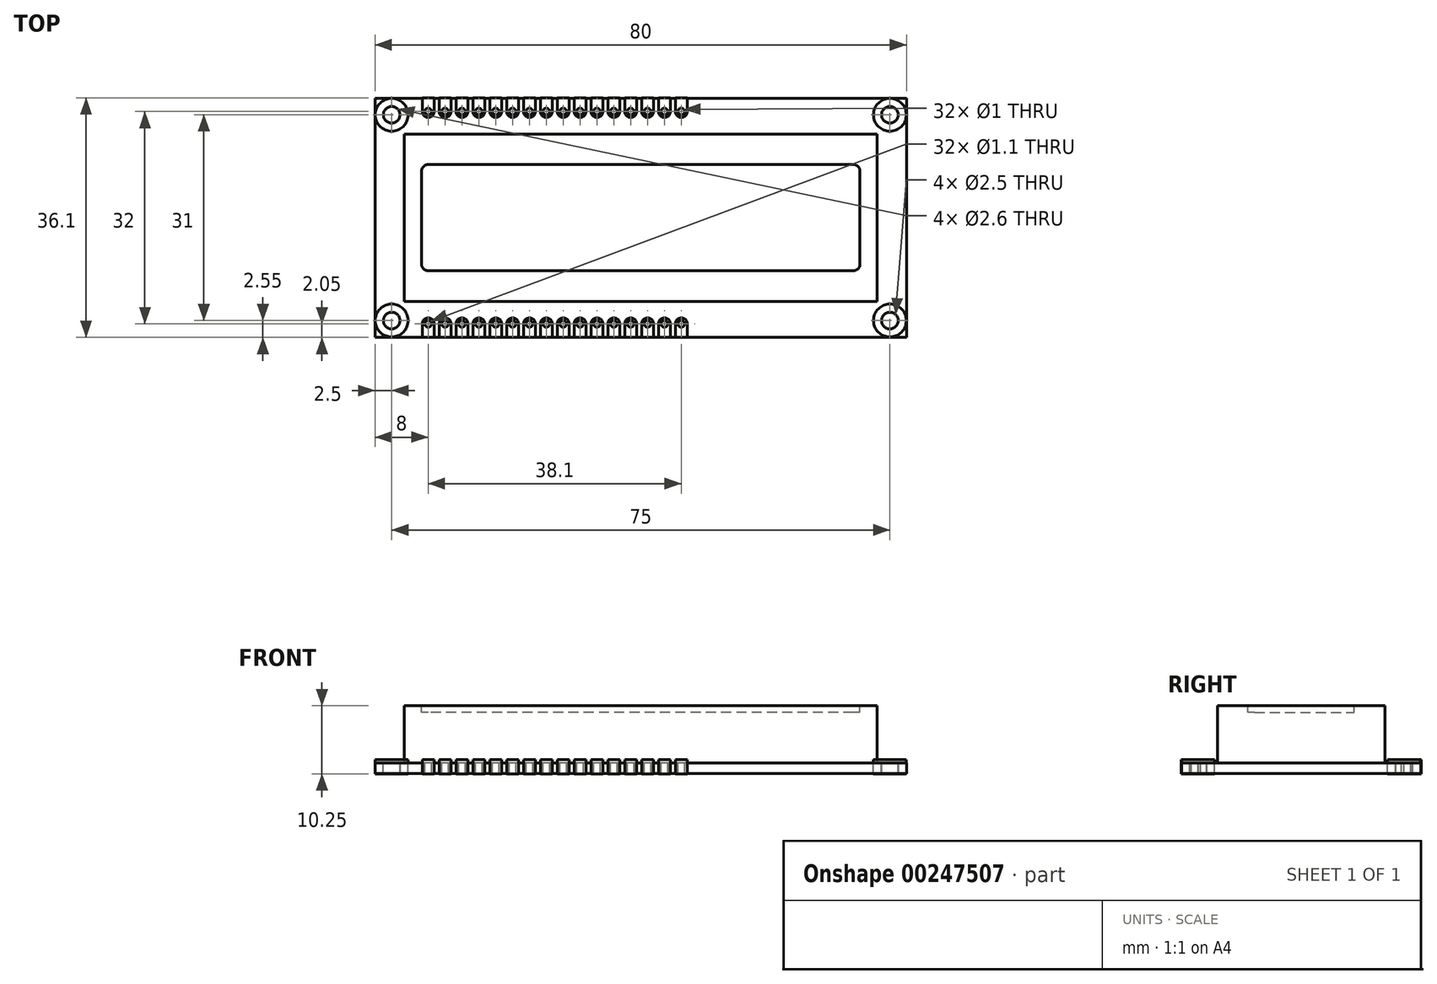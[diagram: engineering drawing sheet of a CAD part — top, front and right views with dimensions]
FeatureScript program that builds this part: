
annotation { "Feature Type Name" : "Feature", "Feature Type Description" : "" }
export const myFeature = defineFeature(function(context is Context, id is Id, definition is map)
    precondition{}
    {
        {
            var Q0;
            Q0=qCreatedBy(makeId("Top.planeOp"),FACE);
            var sketch = newSketch(context, id + "F0", { "sketchPlane" : qUnion([Q0])});
            skLineSegment(sketch, "E0.bottom", {"start": v(40, -18) * mm, "end": v(-40, -18) * mm});
            skLineSegment(sketch, "E0.top", {"start": v(40, 18) * mm, "end": v(-40, 18) * mm});
            skLineSegment(sketch, "E0.left", {"start": v(40, -18) * mm, "end": v(40, 18) * mm});
            skLineSegment(sketch, "E0.right", {"start": v(-40, -18) * mm, "end": v(-40, 18) * mm});
            skPoint(sketch, "E0.middle", {"position": v(0, 0) * mm});
            skSolve(sketch);
        }
        {
            var Q0;
            Q0 = qSketchRegion(id + "F0", true);
            extrude(context, id + "F1", {"entities" : qUnion([Q0]), "depth" : 1.6 * mm});
        }
        {
            var Q0;
            Q0=makeQuery(id+"F1.opExtrude","CAP_FACE",FACE,{"disambiguationData":[OSD([sQuery(id+"F0.wireOp",EDGE,"E0.bottom"),sQuery(id+"F0.wireOp",EDGE,"E0.top"),sQuery(id+"F0.wireOp",EDGE,"E0.left"),sQuery(id+"F0.wireOp",EDGE,"E0.right")])],"isStart":false});
            var sketch = newSketch(context, id + "F2", { "sketchPlane" : qUnion([Q0])});
            skCircle(sketch, "E1", {"center": v(-37.5, 15.5) * mm, "radius": 1.3 * mm});
            skCircle(sketch, "E2.0.1.0", {"center": v(-37.5, -15.5) * mm, "radius": 1.3 * mm});
            skCircle(sketch, "E2.1.0.0", {"center": v(37.5, 15.5) * mm, "radius": 1.3 * mm});
            skCircle(sketch, "E2.1.1.0", {"center": v(37.5, -15.5) * mm, "radius": 1.3 * mm});
            skLineSegment(sketch, "E2.direction1", {"start": v(-37.5, 15.5) * mm, "end": v(37.5, 15.5) * mm, "construction": true});
            skLineSegment(sketch, "E2.direction2", {"start": v(-37.5, 15.5) * mm, "end": v(-37.5, -15.5) * mm, "construction": true});
            skCircle(sketch, "E3", {"center": v(-32, 16) * mm, "radius": 0.55 * mm});
            skCircle(sketch, "E4.0.1.0", {"center": v(-32, -16) * mm, "radius": 0.55 * mm});
            skCircle(sketch, "E4.1.0.0", {"center": v(-29.46, 16) * mm, "radius": 0.55 * mm});
            skCircle(sketch, "E4.1.1.0", {"center": v(-29.46, -16) * mm, "radius": 0.55 * mm});
            skCircle(sketch, "E4.2.0.0", {"center": v(-26.92, 16) * mm, "radius": 0.55 * mm});
            skCircle(sketch, "E4.2.1.0", {"center": v(-26.92, -16) * mm, "radius": 0.55 * mm});
            skCircle(sketch, "E4.3.0.0", {"center": v(-24.38, 16) * mm, "radius": 0.55 * mm});
            skCircle(sketch, "E4.3.1.0", {"center": v(-24.38, -16) * mm, "radius": 0.55 * mm});
            skCircle(sketch, "E4.4.0.0", {"center": v(-21.84, 16) * mm, "radius": 0.55 * mm});
            skCircle(sketch, "E4.4.1.0", {"center": v(-21.84, -16) * mm, "radius": 0.55 * mm});
            skCircle(sketch, "E4.5.0.0", {"center": v(-19.3, 16) * mm, "radius": 0.55 * mm});
            skCircle(sketch, "E4.5.1.0", {"center": v(-19.3, -16) * mm, "radius": 0.55 * mm});
            skCircle(sketch, "E4.6.0.0", {"center": v(-16.76, 16) * mm, "radius": 0.55 * mm});
            skCircle(sketch, "E4.6.1.0", {"center": v(-16.76, -16) * mm, "radius": 0.55 * mm});
            skCircle(sketch, "E4.7.0.0", {"center": v(-14.22, 16) * mm, "radius": 0.55 * mm});
            skCircle(sketch, "E4.7.1.0", {"center": v(-14.22, -16) * mm, "radius": 0.55 * mm});
            skCircle(sketch, "E4.8.0.0", {"center": v(-11.68, 16) * mm, "radius": 0.55 * mm});
            skCircle(sketch, "E4.8.1.0", {"center": v(-11.68, -16) * mm, "radius": 0.55 * mm});
            skCircle(sketch, "E4.9.0.0", {"center": v(-9.14, 16) * mm, "radius": 0.55 * mm});
            skCircle(sketch, "E4.9.1.0", {"center": v(-9.14, -16) * mm, "radius": 0.55 * mm});
            skCircle(sketch, "E4.10.0.0", {"center": v(-6.6, 16) * mm, "radius": 0.55 * mm});
            skCircle(sketch, "E4.10.1.0", {"center": v(-6.6, -16) * mm, "radius": 0.55 * mm});
            skCircle(sketch, "E4.11.0.0", {"center": v(-4.06, 16) * mm, "radius": 0.55 * mm});
            skCircle(sketch, "E4.11.1.0", {"center": v(-4.06, -16) * mm, "radius": 0.55 * mm});
            skCircle(sketch, "E4.12.0.0", {"center": v(-1.52, 16) * mm, "radius": 0.55 * mm});
            skCircle(sketch, "E4.12.1.0", {"center": v(-1.52, -16) * mm, "radius": 0.55 * mm});
            skCircle(sketch, "E4.13.0.0", {"center": v(1.02, 16) * mm, "radius": 0.55 * mm});
            skCircle(sketch, "E4.13.1.0", {"center": v(1.02, -16) * mm, "radius": 0.55 * mm});
            skCircle(sketch, "E4.14.0.0", {"center": v(3.56, 16) * mm, "radius": 0.55 * mm});
            skCircle(sketch, "E4.14.1.0", {"center": v(3.56, -16) * mm, "radius": 0.55 * mm});
            skCircle(sketch, "E4.15.0.0", {"center": v(6.1, 16) * mm, "radius": 0.55 * mm});
            skCircle(sketch, "E4.15.1.0", {"center": v(6.1, -16) * mm, "radius": 0.55 * mm});
            skLineSegment(sketch, "E4.direction1", {"start": v(-32, 16) * mm, "end": v(-29.46, 16) * mm, "construction": true});
            skLineSegment(sketch, "E4.direction2", {"start": v(-32, 16) * mm, "end": v(-32, -16) * mm, "construction": true});
            skSolve(sketch);
        }
        {
            var Q0;
            Q0 = qSketchRegion(id + "F2", true);
            extrude(context, id + "F3", {"entities" : qUnion([Q0]), "operationType" : NewBodyOperationType.REMOVE, "endBound" : BoundingType.THROUGH_ALL, "oppositeDirection" : true, "depth" : 25 * mm});
        }
        {
            var Q0;
            Q0=makeQuery(id+"F1.opExtrude","CAP_FACE",FACE,{"disambiguationData":[OSD([sQuery(id+"F0.wireOp",EDGE,"E0.bottom"),sQuery(id+"F0.wireOp",EDGE,"E0.top"),sQuery(id+"F0.wireOp",EDGE,"E0.left"),sQuery(id+"F0.wireOp",EDGE,"E0.right")])],"isStart":false});
            var sketch = newSketch(context, id + "F4", { "sketchPlane" : qUnion([Q0])});
            skArc(sketch, "E5", {"start": v(-32.9, 16) * mm, "mid": v(-32, 15.1) * mm, "end": v(-31.1, 16) * mm});
            skLineSegment(sketch, "E6", {"start": v(-32.9, 16) * mm, "end": v(-32.9, 18.05) * mm});
            skLineSegment(sketch, "E7", {"start": v(-31.1, 16) * mm, "end": v(-31.1, 18.05) * mm});
            skLineSegment(sketch, "E8", {"start": v(-32.9, 18.05) * mm, "end": v(-31.1, 18.05) * mm});
            skCircle(sketch, "E9", {"center": v(-32, 16) * mm, "radius": 0.5 * mm});
            skLineSegment(sketch, "E10", {"start": v(-40, 0) * mm, "end": v(40, 0) * mm, "construction": true});
            skLineSegment(sketch, "E11.1.0.0", {"start": v(-30.36, 16) * mm, "end": v(-30.36, 18.05) * mm});
            skCircle(sketch, "E11.1.0.1", {"center": v(-29.46, 16) * mm, "radius": 0.5 * mm});
            skArc(sketch, "E11.1.0.2", {"start": v(-30.36, 16) * mm, "mid": v(-29.46, 15.1) * mm, "end": v(-28.56, 16) * mm});
            skLineSegment(sketch, "E11.1.0.3", {"start": v(-28.56, 16) * mm, "end": v(-28.56, 18.05) * mm});
            skLineSegment(sketch, "E11.1.0.4", {"start": v(-30.36, 18.05) * mm, "end": v(-28.56, 18.05) * mm});
            skLineSegment(sketch, "E11.2.0.0", {"start": v(-27.82, 16) * mm, "end": v(-27.82, 18.05) * mm});
            skCircle(sketch, "E11.2.0.1", {"center": v(-26.92, 16) * mm, "radius": 0.5 * mm});
            skArc(sketch, "E11.2.0.2", {"start": v(-27.82, 16) * mm, "mid": v(-26.92, 15.1) * mm, "end": v(-26.02, 16) * mm});
            skLineSegment(sketch, "E11.2.0.3", {"start": v(-26.02, 16) * mm, "end": v(-26.02, 18.05) * mm});
            skLineSegment(sketch, "E11.2.0.4", {"start": v(-27.82, 18.05) * mm, "end": v(-26.02, 18.05) * mm});
            skLineSegment(sketch, "E11.3.0.0", {"start": v(-25.28, 16) * mm, "end": v(-25.28, 18.05) * mm});
            skCircle(sketch, "E11.3.0.1", {"center": v(-24.38, 16) * mm, "radius": 0.5 * mm});
            skArc(sketch, "E11.3.0.2", {"start": v(-25.28, 16) * mm, "mid": v(-24.38, 15.1) * mm, "end": v(-23.48, 16) * mm});
            skLineSegment(sketch, "E11.3.0.3", {"start": v(-23.48, 16) * mm, "end": v(-23.48, 18.05) * mm});
            skLineSegment(sketch, "E11.3.0.4", {"start": v(-25.28, 18.05) * mm, "end": v(-23.48, 18.05) * mm});
            skLineSegment(sketch, "E11.4.0.0", {"start": v(-22.74, 16) * mm, "end": v(-22.74, 18.05) * mm});
            skCircle(sketch, "E11.4.0.1", {"center": v(-21.84, 16) * mm, "radius": 0.5 * mm});
            skArc(sketch, "E11.4.0.2", {"start": v(-22.74, 16) * mm, "mid": v(-21.84, 15.1) * mm, "end": v(-20.94, 16) * mm});
            skLineSegment(sketch, "E11.4.0.3", {"start": v(-20.94, 16) * mm, "end": v(-20.94, 18.05) * mm});
            skLineSegment(sketch, "E11.4.0.4", {"start": v(-22.74, 18.05) * mm, "end": v(-20.94, 18.05) * mm});
            skLineSegment(sketch, "E11.5.0.0", {"start": v(-20.2, 16) * mm, "end": v(-20.2, 18.05) * mm});
            skCircle(sketch, "E11.5.0.1", {"center": v(-19.3, 16) * mm, "radius": 0.5 * mm});
            skArc(sketch, "E11.5.0.2", {"start": v(-20.2, 16) * mm, "mid": v(-19.3, 15.1) * mm, "end": v(-18.4, 16) * mm});
            skLineSegment(sketch, "E11.5.0.3", {"start": v(-18.4, 16) * mm, "end": v(-18.4, 18.05) * mm});
            skLineSegment(sketch, "E11.5.0.4", {"start": v(-20.2, 18.05) * mm, "end": v(-18.4, 18.05) * mm});
            skLineSegment(sketch, "E11.6.0.0", {"start": v(-17.66, 16) * mm, "end": v(-17.66, 18.05) * mm});
            skCircle(sketch, "E11.6.0.1", {"center": v(-16.76, 16) * mm, "radius": 0.5 * mm});
            skArc(sketch, "E11.6.0.2", {"start": v(-17.66, 16) * mm, "mid": v(-16.76, 15.1) * mm, "end": v(-15.86, 16) * mm});
            skLineSegment(sketch, "E11.6.0.3", {"start": v(-15.86, 16) * mm, "end": v(-15.86, 18.05) * mm});
            skLineSegment(sketch, "E11.6.0.4", {"start": v(-17.66, 18.05) * mm, "end": v(-15.86, 18.05) * mm});
            skLineSegment(sketch, "E11.7.0.0", {"start": v(-15.12, 16) * mm, "end": v(-15.12, 18.05) * mm});
            skCircle(sketch, "E11.7.0.1", {"center": v(-14.22, 16) * mm, "radius": 0.5 * mm});
            skArc(sketch, "E11.7.0.2", {"start": v(-15.12, 16) * mm, "mid": v(-14.22, 15.1) * mm, "end": v(-13.32, 16) * mm});
            skLineSegment(sketch, "E11.7.0.3", {"start": v(-13.32, 16) * mm, "end": v(-13.32, 18.05) * mm});
            skLineSegment(sketch, "E11.7.0.4", {"start": v(-15.12, 18.05) * mm, "end": v(-13.32, 18.05) * mm});
            skLineSegment(sketch, "E11.8.0.0", {"start": v(-12.58, 16) * mm, "end": v(-12.58, 18.05) * mm});
            skCircle(sketch, "E11.8.0.1", {"center": v(-11.68, 16) * mm, "radius": 0.5 * mm});
            skArc(sketch, "E11.8.0.2", {"start": v(-12.58, 16) * mm, "mid": v(-11.68, 15.1) * mm, "end": v(-10.78, 16) * mm});
            skLineSegment(sketch, "E11.8.0.3", {"start": v(-10.78, 16) * mm, "end": v(-10.78, 18.05) * mm});
            skLineSegment(sketch, "E11.8.0.4", {"start": v(-12.58, 18.05) * mm, "end": v(-10.78, 18.05) * mm});
            skLineSegment(sketch, "E11.9.0.0", {"start": v(-10.04, 16) * mm, "end": v(-10.04, 18.05) * mm});
            skCircle(sketch, "E11.9.0.1", {"center": v(-9.14, 16) * mm, "radius": 0.5 * mm});
            skArc(sketch, "E11.9.0.2", {"start": v(-10.04, 16) * mm, "mid": v(-9.14, 15.1) * mm, "end": v(-8.24, 16) * mm});
            skLineSegment(sketch, "E11.9.0.3", {"start": v(-8.24, 16) * mm, "end": v(-8.24, 18.05) * mm});
            skLineSegment(sketch, "E11.9.0.4", {"start": v(-10.04, 18.05) * mm, "end": v(-8.24, 18.05) * mm});
            skLineSegment(sketch, "E11.10.0.0", {"start": v(-7.5, 16) * mm, "end": v(-7.5, 18.05) * mm});
            skCircle(sketch, "E11.10.0.1", {"center": v(-6.6, 16) * mm, "radius": 0.5 * mm});
            skArc(sketch, "E11.10.0.2", {"start": v(-7.5, 16) * mm, "mid": v(-6.6, 15.1) * mm, "end": v(-5.7, 16) * mm});
            skLineSegment(sketch, "E11.10.0.3", {"start": v(-5.7, 16) * mm, "end": v(-5.7, 18.05) * mm});
            skLineSegment(sketch, "E11.10.0.4", {"start": v(-7.5, 18.05) * mm, "end": v(-5.7, 18.05) * mm});
            skLineSegment(sketch, "E11.11.0.0", {"start": v(-4.96, 16) * mm, "end": v(-4.96, 18.05) * mm});
            skCircle(sketch, "E11.11.0.1", {"center": v(-4.06, 16) * mm, "radius": 0.5 * mm});
            skArc(sketch, "E11.11.0.2", {"start": v(-4.96, 16) * mm, "mid": v(-4.06, 15.1) * mm, "end": v(-3.16, 16) * mm});
            skLineSegment(sketch, "E11.11.0.3", {"start": v(-3.16, 16) * mm, "end": v(-3.16, 18.05) * mm});
            skLineSegment(sketch, "E11.11.0.4", {"start": v(-4.96, 18.05) * mm, "end": v(-3.16, 18.05) * mm});
            skLineSegment(sketch, "E11.12.0.0", {"start": v(-2.42, 16) * mm, "end": v(-2.42, 18.05) * mm});
            skCircle(sketch, "E11.12.0.1", {"center": v(-1.52, 16) * mm, "radius": 0.5 * mm});
            skArc(sketch, "E11.12.0.2", {"start": v(-2.42, 16) * mm, "mid": v(-1.52, 15.1) * mm, "end": v(-0.62, 16) * mm});
            skLineSegment(sketch, "E11.12.0.3", {"start": v(-0.62, 16) * mm, "end": v(-0.62, 18.05) * mm});
            skLineSegment(sketch, "E11.12.0.4", {"start": v(-2.42, 18.05) * mm, "end": v(-0.62, 18.05) * mm});
            skLineSegment(sketch, "E11.13.0.0", {"start": v(0.12, 16) * mm, "end": v(0.12, 18.05) * mm});
            skCircle(sketch, "E11.13.0.1", {"center": v(1.02, 16) * mm, "radius": 0.5 * mm});
            skArc(sketch, "E11.13.0.2", {"start": v(0.12, 16) * mm, "mid": v(1.02, 15.1) * mm, "end": v(1.92, 16) * mm});
            skLineSegment(sketch, "E11.13.0.3", {"start": v(1.92, 16) * mm, "end": v(1.92, 18.05) * mm});
            skLineSegment(sketch, "E11.13.0.4", {"start": v(0.12, 18.05) * mm, "end": v(1.92, 18.05) * mm});
            skLineSegment(sketch, "E11.14.0.0", {"start": v(2.66, 16) * mm, "end": v(2.66, 18.05) * mm});
            skCircle(sketch, "E11.14.0.1", {"center": v(3.56, 16) * mm, "radius": 0.5 * mm});
            skArc(sketch, "E11.14.0.2", {"start": v(2.66, 16) * mm, "mid": v(3.56, 15.1) * mm, "end": v(4.46, 16) * mm});
            skLineSegment(sketch, "E11.14.0.3", {"start": v(4.46, 16) * mm, "end": v(4.46, 18.05) * mm});
            skLineSegment(sketch, "E11.14.0.4", {"start": v(2.66, 18.05) * mm, "end": v(4.46, 18.05) * mm});
            skLineSegment(sketch, "E11.15.0.0", {"start": v(5.2, 16) * mm, "end": v(5.2, 18.05) * mm});
            skCircle(sketch, "E11.15.0.1", {"center": v(6.1, 16) * mm, "radius": 0.5 * mm});
            skArc(sketch, "E11.15.0.2", {"start": v(5.2, 16) * mm, "mid": v(6.1, 15.1) * mm, "end": v(7, 16) * mm});
            skLineSegment(sketch, "E11.15.0.3", {"start": v(7, 16) * mm, "end": v(7, 18.05) * mm});
            skLineSegment(sketch, "E11.15.0.4", {"start": v(5.2, 18.05) * mm, "end": v(7, 18.05) * mm});
            skLineSegment(sketch, "E11.direction1", {"start": v(-32.9, 16) * mm, "end": v(-30.36, 16) * mm, "construction": true});
            skCircle(sketch, "E12.MirrorC", {"center": v(-21.84, -16) * mm, "radius": 0.5 * mm});
            skCircle(sketch, "E13.MirrorC", {"center": v(-9.14, -16) * mm, "radius": 0.5 * mm});
            skCircle(sketch, "E14.MirrorC", {"center": v(3.56, -16) * mm, "radius": 0.5 * mm});
            skCircle(sketch, "E15.MirrorC", {"center": v(-6.6, -16) * mm, "radius": 0.5 * mm});
            skCircle(sketch, "E16.MirrorC", {"center": v(6.1, -16) * mm, "radius": 0.5 * mm});
            skCircle(sketch, "E17.MirrorC", {"center": v(-29.46, -16) * mm, "radius": 0.5 * mm});
            skCircle(sketch, "E18.MirrorC", {"center": v(-26.92, -16) * mm, "radius": 0.5 * mm});
            skCircle(sketch, "E19.MirrorC", {"center": v(-14.22, -16) * mm, "radius": 0.5 * mm});
            skCircle(sketch, "E20.MirrorC", {"center": v(-1.52, -16) * mm, "radius": 0.5 * mm});
            skCircle(sketch, "E21.MirrorC", {"center": v(-16.76, -16) * mm, "radius": 0.5 * mm});
            skCircle(sketch, "E22.MirrorC", {"center": v(-4.06, -16) * mm, "radius": 0.5 * mm});
            skLineSegment(sketch, "E23.MirrorCS", {"start": v(-32.9, -16) * mm, "end": v(-30.36, -16) * mm, "construction": true});
            skCircle(sketch, "E24.MirrorC", {"center": v(-32, -16) * mm, "radius": 0.5 * mm});
            skCircle(sketch, "E25.MirrorC", {"center": v(-24.38, -16) * mm, "radius": 0.5 * mm});
            skLineSegment(sketch, "E26.MirrorCS", {"start": v(0.12, -18.05) * mm, "end": v(1.92, -18.05) * mm});
            skLineSegment(sketch, "E27.MirrorCS", {"start": v(-5.7, -16) * mm, "end": v(-5.7, -18.05) * mm});
            skLineSegment(sketch, "E28.MirrorCS", {"start": v(-10.78, -16) * mm, "end": v(-10.78, -18.05) * mm});
            skLineSegment(sketch, "E29.MirrorCS", {"start": v(-0.62, -16) * mm, "end": v(-0.62, -18.05) * mm});
            skLineSegment(sketch, "E30.MirrorCS", {"start": v(-30.36, -18.05) * mm, "end": v(-28.56, -18.05) * mm});
            skLineSegment(sketch, "E31.MirrorCS", {"start": v(7, -16) * mm, "end": v(7, -18.05) * mm});
            skLineSegment(sketch, "E32.MirrorCS", {"start": v(1.92, -16) * mm, "end": v(1.92, -18.05) * mm});
            skLineSegment(sketch, "E33.MirrorCS", {"start": v(-7.5, -16) * mm, "end": v(-7.5, -18.05) * mm});
            skLineSegment(sketch, "E34.MirrorCS", {"start": v(-27.82, -18.05) * mm, "end": v(-26.02, -18.05) * mm});
            skLineSegment(sketch, "E35.MirrorCS", {"start": v(-2.42, -18.05) * mm, "end": v(-0.62, -18.05) * mm});
            skLineSegment(sketch, "E36.MirrorCS", {"start": v(-15.12, -18.05) * mm, "end": v(-13.32, -18.05) * mm});
            skCircle(sketch, "E37.MirrorC", {"center": v(-11.68, -16) * mm, "radius": 0.5 * mm});
            skLineSegment(sketch, "E38.MirrorCS", {"start": v(-4.96, -16) * mm, "end": v(-4.96, -18.05) * mm});
            skLineSegment(sketch, "E39.MirrorCS", {"start": v(-20.94, -16) * mm, "end": v(-20.94, -18.05) * mm});
            skLineSegment(sketch, "E40.MirrorCS", {"start": v(2.66, -18.05) * mm, "end": v(4.46, -18.05) * mm});
            skLineSegment(sketch, "E41.MirrorCS", {"start": v(2.66, -16) * mm, "end": v(2.66, -18.05) * mm});
            skLineSegment(sketch, "E42.MirrorCS", {"start": v(-32.9, -18.05) * mm, "end": v(-31.1, -18.05) * mm});
            skLineSegment(sketch, "E43.MirrorCS", {"start": v(-20.2, -16) * mm, "end": v(-20.2, -18.05) * mm});
            skLineSegment(sketch, "E44.MirrorCS", {"start": v(-13.32, -16) * mm, "end": v(-13.32, -18.05) * mm});
            skLineSegment(sketch, "E45.MirrorCS", {"start": v(-12.58, -16) * mm, "end": v(-12.58, -18.05) * mm});
            skCircle(sketch, "E46.MirrorC", {"center": v(-19.3, -16) * mm, "radius": 0.5 * mm});
            skLineSegment(sketch, "E47.MirrorCS", {"start": v(-31.1, -16) * mm, "end": v(-31.1, -18.05) * mm});
            skCircle(sketch, "E48.MirrorC", {"center": v(1.02, -16) * mm, "radius": 0.5 * mm});
            skLineSegment(sketch, "E49.MirrorCS", {"start": v(-18.4, -16) * mm, "end": v(-18.4, -18.05) * mm});
            skLineSegment(sketch, "E50.MirrorCS", {"start": v(-20.2, -18.05) * mm, "end": v(-18.4, -18.05) * mm});
            skLineSegment(sketch, "E51.MirrorCS", {"start": v(0.12, -16) * mm, "end": v(0.12, -18.05) * mm});
            skLineSegment(sketch, "E52.MirrorCS", {"start": v(4.46, -16) * mm, "end": v(4.46, -18.05) * mm});
            skLineSegment(sketch, "E53.MirrorCS", {"start": v(-3.16, -16) * mm, "end": v(-3.16, -18.05) * mm});
            skLineSegment(sketch, "E54.MirrorCS", {"start": v(-17.66, -18.05) * mm, "end": v(-15.86, -18.05) * mm});
            skLineSegment(sketch, "E55.MirrorCS", {"start": v(-10.04, -16) * mm, "end": v(-10.04, -18.05) * mm});
            skLineSegment(sketch, "E56.MirrorCS", {"start": v(-22.74, -16) * mm, "end": v(-22.74, -18.05) * mm});
            skLineSegment(sketch, "E57.MirrorCS", {"start": v(-8.24, -16) * mm, "end": v(-8.24, -18.05) * mm});
            skLineSegment(sketch, "E58.MirrorCS", {"start": v(-15.86, -16) * mm, "end": v(-15.86, -18.05) * mm});
            skLineSegment(sketch, "E59.MirrorCS", {"start": v(-32.9, -16) * mm, "end": v(-32.9, -18.05) * mm});
            skLineSegment(sketch, "E60.MirrorCS", {"start": v(-27.82, -16) * mm, "end": v(-27.82, -18.05) * mm});
            skLineSegment(sketch, "E61.MirrorCS", {"start": v(-10.04, -18.05) * mm, "end": v(-8.24, -18.05) * mm});
            skLineSegment(sketch, "E62.MirrorCS", {"start": v(-15.12, -16) * mm, "end": v(-15.12, -18.05) * mm});
            skLineSegment(sketch, "E63.MirrorCS", {"start": v(-23.48, -16) * mm, "end": v(-23.48, -18.05) * mm});
            skLineSegment(sketch, "E64.MirrorCS", {"start": v(-28.56, -16) * mm, "end": v(-28.56, -18.05) * mm});
            skLineSegment(sketch, "E65.MirrorCS", {"start": v(-17.66, -16) * mm, "end": v(-17.66, -18.05) * mm});
            skLineSegment(sketch, "E66.MirrorCS", {"start": v(-25.28, -18.05) * mm, "end": v(-23.48, -18.05) * mm});
            skLineSegment(sketch, "E67.MirrorCS", {"start": v(-22.74, -18.05) * mm, "end": v(-20.94, -18.05) * mm});
            skLineSegment(sketch, "E68.MirrorCS", {"start": v(-30.36, -16) * mm, "end": v(-30.36, -18.05) * mm});
            skLineSegment(sketch, "E69.MirrorCS", {"start": v(-25.28, -16) * mm, "end": v(-25.28, -18.05) * mm});
            skLineSegment(sketch, "E70.MirrorCS", {"start": v(-12.58, -18.05) * mm, "end": v(-10.78, -18.05) * mm});
            skLineSegment(sketch, "E71.MirrorCS", {"start": v(-2.42, -16) * mm, "end": v(-2.42, -18.05) * mm});
            skLineSegment(sketch, "E72.MirrorCS", {"start": v(-4.96, -18.05) * mm, "end": v(-3.16, -18.05) * mm});
            skLineSegment(sketch, "E73.MirrorCS", {"start": v(-7.5, -18.05) * mm, "end": v(-5.7, -18.05) * mm});
            skLineSegment(sketch, "E74.MirrorCS", {"start": v(5.2, -18.05) * mm, "end": v(7, -18.05) * mm});
            skLineSegment(sketch, "E75.MirrorCS", {"start": v(-26.02, -16) * mm, "end": v(-26.02, -18.05) * mm});
            skLineSegment(sketch, "E76.MirrorCS", {"start": v(5.2, -16) * mm, "end": v(5.2, -18.05) * mm});
            skArc(sketch, "E77.MirrorCS", {"start": v(-30.36, -16) * mm, "mid": v(-29.46, -15.1) * mm, "end": v(-28.56, -16) * mm});
            skArc(sketch, "E78.MirrorCS", {"start": v(-27.82, -16) * mm, "mid": v(-26.92, -15.1) * mm, "end": v(-26.02, -16) * mm});
            skArc(sketch, "E79.MirrorCS", {"start": v(-20.2, -16) * mm, "mid": v(-19.3, -15.1) * mm, "end": v(-18.4, -16) * mm});
            skArc(sketch, "E80.MirrorCS", {"start": v(-2.42, -16) * mm, "mid": v(-1.52, -15.1) * mm, "end": v(-0.62, -16) * mm});
            skArc(sketch, "E81.MirrorCS", {"start": v(-17.66, -16) * mm, "mid": v(-16.76, -15.1) * mm, "end": v(-15.86, -16) * mm});
            skArc(sketch, "E82.MirrorCS", {"start": v(0.12, -16) * mm, "mid": v(1.02, -15.1) * mm, "end": v(1.92, -16) * mm});
            skArc(sketch, "E83.MirrorCS", {"start": v(-32.9, -16) * mm, "mid": v(-32, -15.1) * mm, "end": v(-31.1, -16) * mm});
            skArc(sketch, "E84.MirrorCS", {"start": v(-22.74, -16) * mm, "mid": v(-21.84, -15.1) * mm, "end": v(-20.94, -16) * mm});
            skArc(sketch, "E85.MirrorCS", {"start": v(-25.28, -16) * mm, "mid": v(-24.38, -15.1) * mm, "end": v(-23.48, -16) * mm});
            skArc(sketch, "E86.MirrorCS", {"start": v(-12.58, -16) * mm, "mid": v(-11.68, -15.1) * mm, "end": v(-10.78, -16) * mm});
            skArc(sketch, "E87.MirrorCS", {"start": v(-10.04, -16) * mm, "mid": v(-9.14, -15.1) * mm, "end": v(-8.24, -16) * mm});
            skArc(sketch, "E88.MirrorCS", {"start": v(-15.12, -16) * mm, "mid": v(-14.22, -15.1) * mm, "end": v(-13.32, -16) * mm});
            skArc(sketch, "E89.MirrorCS", {"start": v(-7.5, -16) * mm, "mid": v(-6.6, -15.1) * mm, "end": v(-5.7, -16) * mm});
            skArc(sketch, "E90.MirrorCS", {"start": v(5.2, -16) * mm, "mid": v(6.1, -15.1) * mm, "end": v(7, -16) * mm});
            skArc(sketch, "E91.MirrorCS", {"start": v(-4.96, -16) * mm, "mid": v(-4.06, -15.1) * mm, "end": v(-3.16, -16) * mm});
            skArc(sketch, "E92.MirrorCS", {"start": v(2.66, -16) * mm, "mid": v(3.56, -15.1) * mm, "end": v(4.46, -16) * mm});
            skCircle(sketch, "E93", {"center": v(-37.5, 15.5) * mm, "radius": 2.48 * mm});
            skCircle(sketch, "E94", {"center": v(-37.5, 15.5) * mm, "radius": 1.25 * mm});
            skCircle(sketch, "E95.0.1.0", {"center": v(-37.5, -15.5) * mm, "radius": 2.48 * mm});
            skCircle(sketch, "E95.0.1.1", {"center": v(-37.5, -15.5) * mm, "radius": 1.25 * mm});
            skCircle(sketch, "E95.1.0.0", {"center": v(37.5, 15.5) * mm, "radius": 2.48 * mm});
            skCircle(sketch, "E95.1.0.1", {"center": v(37.5, 15.5) * mm, "radius": 1.25 * mm});
            skCircle(sketch, "E95.1.1.0", {"center": v(37.5, -15.5) * mm, "radius": 2.48 * mm});
            skCircle(sketch, "E95.1.1.1", {"center": v(37.5, -15.5) * mm, "radius": 1.25 * mm});
            skLineSegment(sketch, "E95.direction1", {"start": v(-37.5, 15.5) * mm, "end": v(37.5, 15.5) * mm, "construction": true});
            skLineSegment(sketch, "E95.direction2", {"start": v(-37.5, 15.5) * mm, "end": v(-37.5, -15.5) * mm, "construction": true});
            skSolve(sketch);
        }
        {
            var Q0;
            Q0 = qSketchRegion(id + "F4", true);
            extrude(context, id + "F5", {"entities" : qUnion([Q0]), "oppositeDirection" : true, "depth" : 1.65 * mm, "hasSecondDirection" : true, "secondDirectionOppositeDirection" : false, "secondDirectionDepth" : .5 * mm});
        }
        {
            var Q0;
            Q0=makeQuery(id+"F1.opExtrude","CAP_FACE",FACE,{"disambiguationData":[OSD([sQuery(id+"F0.wireOp",EDGE,"E0.bottom"),sQuery(id+"F0.wireOp",EDGE,"E0.top"),sQuery(id+"F0.wireOp",EDGE,"E0.left"),sQuery(id+"F0.wireOp",EDGE,"E0.right")])],"isStart":false});
            var sketch = newSketch(context, id + "F6", { "sketchPlane" : qUnion([Q0])});
            skLineSegment(sketch, "E96.bottom", {"start": v(35.6, -12.6) * mm, "end": v(-35.6, -12.6) * mm});
            skLineSegment(sketch, "E96.top", {"start": v(35.6, 12.6) * mm, "end": v(-35.6, 12.6) * mm});
            skLineSegment(sketch, "E96.left", {"start": v(35.6, -12.6) * mm, "end": v(35.6, 12.6) * mm});
            skLineSegment(sketch, "E96.right", {"start": v(-35.6, -12.6) * mm, "end": v(-35.6, 12.6) * mm});
            skPoint(sketch, "E96.middle", {"position": v(0, 0) * mm});
            skSolve(sketch);
        }
        {
            var Q0;
            Q0 = qSketchRegion(id + "F6", true);
            extrude(context, id + "F7", {"entities" : qUnion([Q0]), "depth" : 8.6 * mm});
        }
        {
            var Q0;
            Q0=makeQuery(id+"F7.opExtrude","CAP_FACE",FACE,{"disambiguationData":[OSD([sQuery(id+"F6.wireOp",EDGE,"E96.bottom"),sQuery(id+"F6.wireOp",EDGE,"E96.top"),sQuery(id+"F6.wireOp",EDGE,"E96.left"),sQuery(id+"F6.wireOp",EDGE,"E96.right")])],"isStart":false});
            var sketch = newSketch(context, id + "F8", { "sketchPlane" : qUnion([Q0])});
            skLineSegment(sketch, "E97.bottom", {"start": v(32, -8) * mm, "end": v(-32, -8) * mm});
            skLineSegment(sketch, "E97.top", {"start": v(32, 8) * mm, "end": v(-32, 8) * mm});
            skLineSegment(sketch, "E97.left", {"start": v(33, -7) * mm, "end": v(33, 7) * mm});
            skLineSegment(sketch, "E97.right", {"start": v(-33, -7) * mm, "end": v(-33, 7) * mm});
            skPoint(sketch, "E97.middle", {"position": v(0, 0) * mm});
            skPoint(sketch, "E98.visualSharp", {"position": v(-33, 8) * mm});
            skArc(sketch, "E98.filletArc", {"start": v(-32, 8) * mm, "mid": v(-32.7, 7.7) * mm, "end": v(-33, 7) * mm});
            skPoint(sketch, "E99.visualSharp", {"position": v(33, 8) * mm});
            skArc(sketch, "E99.filletArc", {"start": v(33, 7) * mm, "mid": v(32.7, 7.7) * mm, "end": v(32, 8) * mm});
            skPoint(sketch, "E100.visualSharp", {"position": v(33, -8) * mm});
            skArc(sketch, "E100.filletArc", {"start": v(32, -8) * mm, "mid": v(32.7, -7.7) * mm, "end": v(33, -7) * mm});
            skPoint(sketch, "E101.visualSharp", {"position": v(-33, -8) * mm});
            skArc(sketch, "E101.filletArc", {"start": v(-33, -7) * mm, "mid": v(-32.7, -7.7) * mm, "end": v(-32, -8) * mm});
            skSolve(sketch);
        }
        {
            var Q0;
            Q0 = qSketchRegion(id + "F8", true);
            extrude(context, id + "F9", {"entities" : qUnion([Q0]), "operationType" : NewBodyOperationType.REMOVE, "oppositeDirection" : true, "depth" : 1 * mm});
        }
    });
